# Revit family: FP-Revit20-DD24ST4NX9-Dishdrawer-0-90004787A-US-CA
name_source: partatom
category: Specialty Equipment
units: mm (PartAtom-declared; Revit-internal decimal feet)

## family parameters
Always vertical = No
Cut with Voids When Loaded = Yes
OmniClass Number = 23.45.00.00
OmniClass Title = Sanitary, Laundry, and Cleaning Equipment
Part Type = Normal
Room Calculation Point = No
Round Connector Dimension = Use Diameter
Shared = No
Work Plane-Based = Yes

## types (1)
- DD24ST4NX9
    Cavity - Depth = 580 mm  [stored 1.90289 ft]
    Cavity - Height = 456 mm  [stored 1.49606 ft]
    Cavity - Width = 600 mm
    Connector note - Electrical = 100 - 120V, 60Hz, 10 A
    Default Elevation = 1219 mm
    Description = Series 9, Tall Single DishDrawer™ Dishwasher
    Manufacturer = Fisher & Paykel Appliances
    Material - Body = Fisher & Paykel - Grey
    Material - Door Panel = Fisher & Paykel - Stainless Steel
    Material - Handle = Fisher & Paykel - Stainless Steel
    Model = DD24ST4NX9
    Product - Depth = 573 mm  [stored 1.87992 ft]
    Product - Height = 453 mm  [stored 1.48622 ft]
    Product - Width = 599 mm  [stored 1.96522 ft]
    URL = www.fisherpaykel.com

note: [stored X ft] marks values corroborated as IEEE doubles in the binary element streams (Revit-internal decimal feet)

## geometry (parser evidence)
native form markers: Sweep x2
no freeform markers — native parametric forms only
